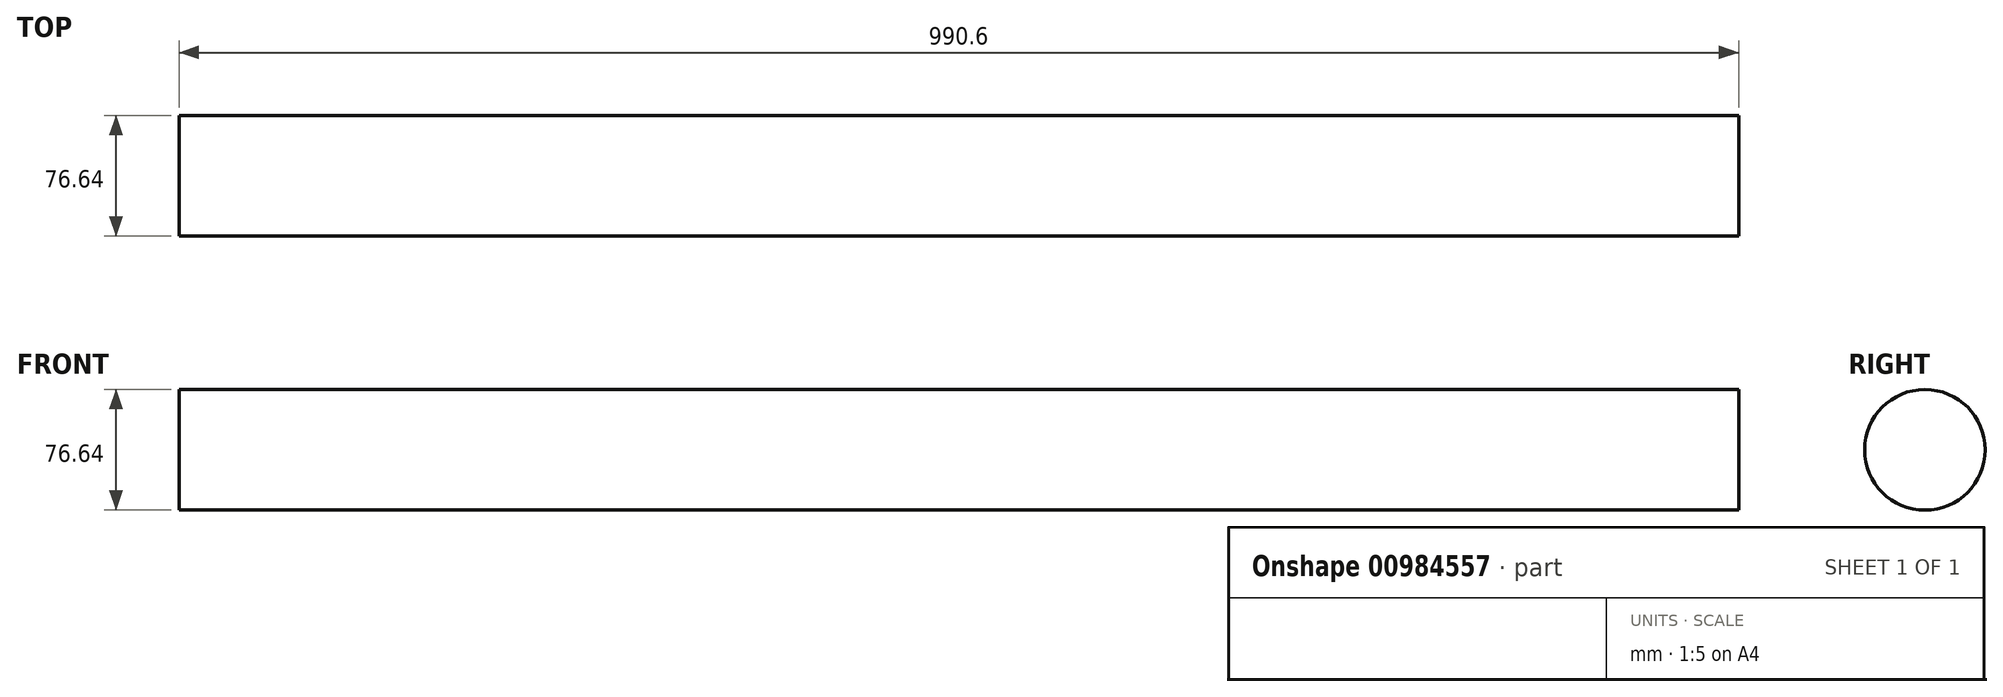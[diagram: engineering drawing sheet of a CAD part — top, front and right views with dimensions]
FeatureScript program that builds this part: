
annotation { "Feature Type Name" : "Feature", "Feature Type Description" : "" }
export const myFeature = defineFeature(function(context is Context, id is Id, definition is map)
    precondition{}
    {
        {
            var Q0;
            Q0=qCreatedBy(makeId("Right.planeOp"),FACE);
            var sketch = newSketch(context, id + "F0", { "sketchPlane" : qUnion([Q0])});
            skCircle(sketch, "E0", {"center": v(0, 0) * mm, "radius": 38.32 * mm});
            skSolve(sketch);
        }
        {
            var Q0;
            Q0=makeQuery(id+"F0.imprint","IMPRINT",FACE,{"disambiguationData":[TD([[makeQuery(id+"F0.imprint","IMPRINT",EDGE,{"derivedFrom":sQuery(id+"F0.wireOp",EDGE,"E0")}),1.0]])]});
            extrude(context, id + "F1", {"entities" : qUnion([Q0]), "oppositeDirection" : true, "depth" : 990.6 * mm, "offsetDistance" : 25.4 * mm});
        }
    });
